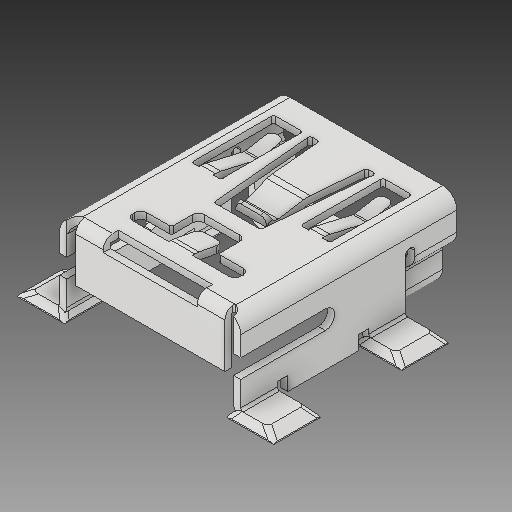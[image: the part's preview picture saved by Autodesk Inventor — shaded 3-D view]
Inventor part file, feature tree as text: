
AUTODESK INVENTOR PART (.ipt)
format: ipt  version: 2019.4 (Build 234330000, 330)  size: 392,704 bytes
history: native  units: mm
features: fillet x1
ambient origin geometry x8: Origin, YZ Plane, XZ Plane, XY Plane, X Axis, Y Axis, Z Axis, Center Point
bodies: Solid1 (feature_tree)
feature tree (1):
  fillet  "Fillet14"  [1 undecoded]
note: 1 required parameter value undecoded (feature->parameter linkage not recoverable at this tier; creation-order binding heuristic only, values carry confidence <= 0.55)
